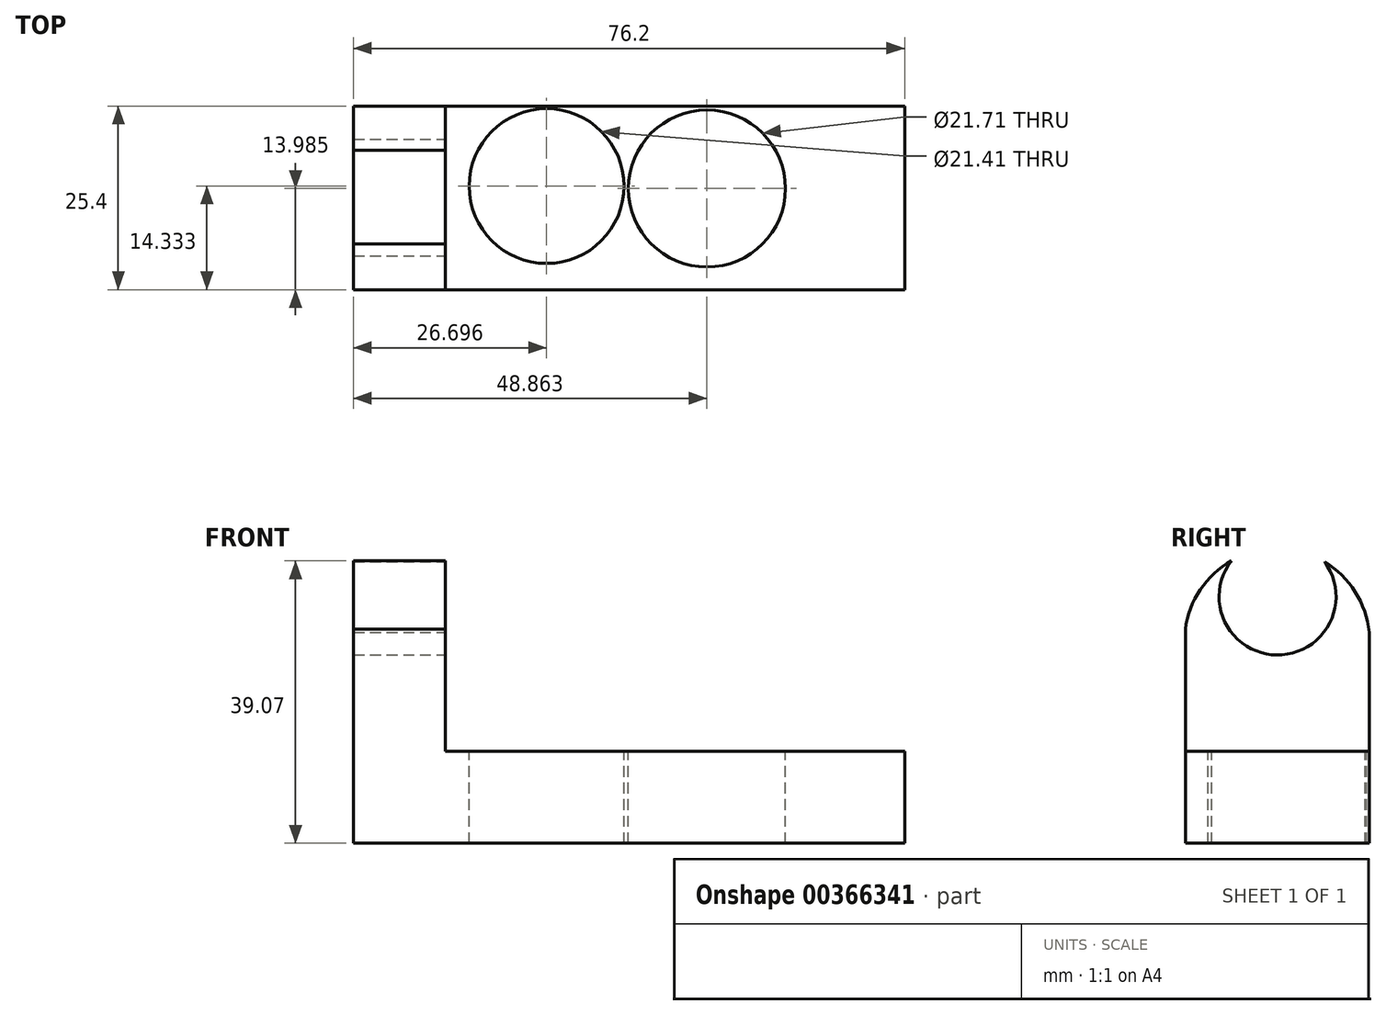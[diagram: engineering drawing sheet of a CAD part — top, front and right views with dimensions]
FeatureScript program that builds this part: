
annotation { "Feature Type Name" : "Feature", "Feature Type Description" : "" }
export const myFeature = defineFeature(function(context is Context, id is Id, definition is map)
    precondition{}
    {
        {
            var Q0;
            Q0=qCreatedBy(makeId("Front.planeOp"),FACE);
            var sketch = newSketch(context, id + "F0", { "sketchPlane" : qUnion([Q0])});
            skLineSegment(sketch, "E0", {"start": v(-33.27, 44.45) * mm, "end": v(-33.27, 0) * mm});
            skLineSegment(sketch, "E1", {"start": v(-33.27, 0) * mm, "end": v(42.93, 0) * mm});
            skLineSegment(sketch, "E2", {"start": v(42.93, 0) * mm, "end": v(42.93, 12.7) * mm});
            skLineSegment(sketch, "E3", {"start": v(42.93, 12.7) * mm, "end": v(-20.57, 12.7) * mm});
            skLineSegment(sketch, "E4", {"start": v(-20.57, 12.7) * mm, "end": v(-20.57, 44.45) * mm});
            skLineSegment(sketch, "E5", {"start": v(-20.57, 44.45) * mm, "end": v(-33.27, 44.45) * mm});
            skSolve(sketch);
        }
        {
            var Q0;
            Q0 = qSketchRegion(id + "F0", true);
            extrude(context, id + "F1", {"entities" : qUnion([Q0]), "depth" : 25.4 * mm});
        }
        {
            var Q0;
            Q0=makeQuery(id+"F1.opExtrude","SWEPT_FACE",FACE,{"disambiguationData":[OSD([sQuery(id+"F0.wireOp",EDGE,"E3")])]});
            var sketch = newSketch(context, id + "F2", { "sketchPlane" : qUnion([Q0])});
            skSolve(sketch);
        }
        {
            var Q0;
            Q0=makeQuery(id+"F1.opExtrude","SWEPT_FACE",FACE,{"disambiguationData":[OSD([sQuery(id+"F0.wireOp",EDGE,"E4")])]});
            var sketch = newSketch(context, id + "F3", { "sketchPlane" : qUnion([Q0])});
            skArc(sketch, "E6", {"start": v(0, 26.74) * mm, "mid": v(-12.92, 40.74) * mm, "end": v(-25.4, 26.33) * mm});
            skSolve(sketch);
        }
        {
            var Q0;
            Q0 = qSketchRegion(id + "F3", true);
            var Q1;
            {var subQ1=sQuery(id+"F0.wireOp",EDGE,"E4");var subQ6=makeQuery(id+"F1.opExtrude","SWEPT_EDGE",EDGE,{"disambiguationData":[OSD([subQ1,sQuery(id+"F0.wireOp",EDGE,"E5")])]});Q1=makeQuery(id+"F3.imprint","IMPRINT",FACE,{"disambiguationData":[TD([[makeQuery(id+"F3.imprint","IMPRINT",EDGE,{"derivedFrom":subQ6}),-1.0]])]});}
            extrude(context, id + "F4", {"entities" : qUnion([Q0, Q1]), "operationType" : NewBodyOperationType.REMOVE, "oppositeDirection" : true, "depth" : 25.4 * mm});
        }
        {
            var Q0;
            Q0=makeQuery(id+"F1.opExtrude","SWEPT_FACE",FACE,{"disambiguationData":[OSD([sQuery(id+"F0.wireOp",EDGE,"E4")])]});
            var sketch = newSketch(context, id + "F5", { "sketchPlane" : qUnion([Q0])});
            skArc(sketch, "E7", {"start": v(-19.04, 39.07) * mm, "mid": v(-12.74, 26.05) * mm, "end": v(-6.15, 38.93) * mm});
            skSolve(sketch);
        }
        {
            var Q0;
            Q0 = qSketchRegion(id + "F5", true);
            var Q1;
            {var subQ0=sQuery(id+"F5.wireOp",EDGE,"E7");Q1=makeQuery(id+"F5.imprint","IMPRINT",FACE,{"disambiguationData":[TD([[makeQuery(id+"F5.imprint","IMPRINT",EDGE,{"derivedFrom":subQ0}),1.0]])]});}
            extrude(context, id + "F6", {"entities" : qUnion([Q0, Q1]), "operationType" : NewBodyOperationType.REMOVE, "oppositeDirection" : true, "depth" : 25.4 * mm});
        }
        {
            var Q0;
            {var subQ0=sQuery(id+"F0.wireOp",EDGE,"E3");Q0=makeQuery(id+"F2.imprint","IMPRINT",FACE,{"disambiguationData":[TD([[makeQuery(id+"F2.imprint","IMPRINT",EDGE,{"derivedFrom":makeQuery(id+"F1.opExtrude","CAP_EDGE",EDGE,{"disambiguationData":[OSD([subQ0])],"isStart":true})}),1.0]])]});}
            var sketch = newSketch(context, id + "F7", { "sketchPlane" : qUnion([Q0])});
            skCircle(sketch, "E8", {"center": v(-6.57, -11.07) * mm, "radius": 10.7 * mm});
            skCircle(sketch, "E9", {"center": v(15.6, -11.41) * mm, "radius": 10.85 * mm});
            skSolve(sketch);
        }
        {
            var Q0;
            Q0 = qSketchRegion(id + "F7", true);
            extrude(context, id + "F8", {"entities" : qUnion([Q0]), "operationType" : NewBodyOperationType.REMOVE, "oppositeDirection" : true, "depth" : 25.4 * mm});
        }
    });
